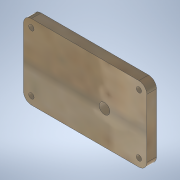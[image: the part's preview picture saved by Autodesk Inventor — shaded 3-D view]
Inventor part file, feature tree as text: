
AUTODESK INVENTOR PART (.ipt)
format: ipt  version: 2020.3 (Build 243373000, 373)  size: 210,432 bytes
history: native  units: mm
features: sketch x4, hole x3, other x1, extrude x1, fillet x1
ambient origin geometry x8: Origin, YZ Plane, XZ Plane, XY Plane, X Axis, Y Axis, Z Axis, Center Point
bodies: Body1 (feature_tree)
feature tree (10):
  other  "ソリッド1"
  extrude  "押し出し1"  Depth=70.0mm
  hole  "穴1"  [1 undecoded]
  fillet  "フィレット1"  Radius=5.5mm
  hole  "穴2"  [1 undecoded]
  hole  "穴3"  [1 undecoded]
  sketch  "スケッチ1"
  sketch  "スケッチ2"
  sketch  "スケッチ3"
  sketch  "スケッチ4"
note: 3 required parameter values undecoded (feature->parameter linkage not recoverable at this tier; creation-order binding heuristic only, values carry confidence <= 0.55)
